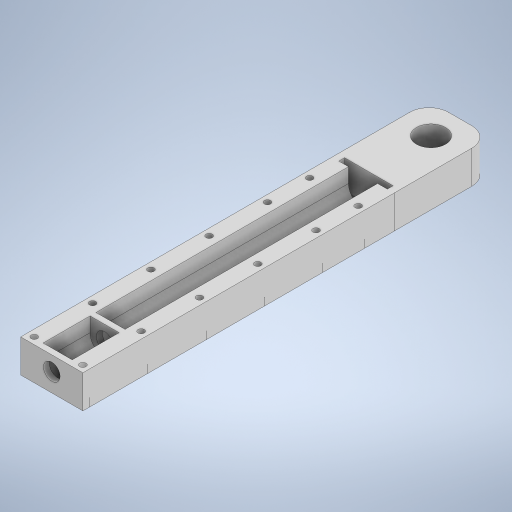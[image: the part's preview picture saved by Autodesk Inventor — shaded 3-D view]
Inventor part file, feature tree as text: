
AUTODESK INVENTOR PART (.ipt)
format: ipt  version: 2023 (Build 270158000, 158)  size: 453,120 bytes
history: native  units: mm
features: sketch x10, extrude x7, hole x3, fillet x1, projected_geometry x1
ambient origin geometry x8: Origin, YZ Plane, XZ Plane, XY Plane, X Axis, Y Axis, Z Axis, Center Point
bodies: Solid1 (feature_tree)
feature tree (22):
  extrude  "Extrusion1"  Depth=24.2mm TaperAngle=0.0deg
  extrude  "Extrusion3"  Depth=2.0mm
  extrude  "Extrusion4"  Depth=3.0mm TaperAngle=0.0deg
  extrude  "Extrusion5"  Depth=130.0mm TaperAngle=0.0deg
  hole  "Hole1"  [1 undecoded]
  hole  "Hole3"  [1 undecoded]
  extrude  "Extrusion6"  Depth=3.5mm
  extrude  "Extrusion7"  Depth=6.0mm
  fillet  "Fillet1"  Radius=50.0mm
  hole  "Hole4"  [1 undecoded]
  extrude  "Extrusion8"  Depth=20.0mm
  sketch  "Sketch1"  dims[d0=15.0mm d3=24.2mm d4=0.0mm]
  sketch  "Sketch2"  dims[d5=32.0mm d6=2.0mm]
  projected_geometry  "Projected Loop1"
  sketch  "Sketch4"  dims[d10=8.5mm d11=3.0mm d12=0.0mm]
  sketch  "Sketch5"  dims[d13=3.0mm d14=0.0mm d15=130.0mm d16=0.0mm]
  sketch  "Sketch6"  dims[d17=3.5mm d18=3.5mm]
  sketch  "Sketch7"  dims[d19=2.38125mm d20=6.0mm d21=4.0mm d22=2.0mm d23=90.0deg d24=10.0mm d25=20.594885mm d27=3.5mm]
  sketch  "Sketch8"  dims[d42=50.0mm d44=30.0mm d45=10.0mm d47=10.0mm d49=3.5mm]
  sketch  "Sketch9"  dims[d50=15.0mm]
  sketch  "Sketch10"  dims[d51=3.175mm d52=6.0mm d53=4.0mm d54=2.0mm d55=90.0deg d56=10.0mm d57=20.594885mm d58=6.0mm]
  sketch  "Sketch11"  dims[d59=20.0mm d61=25.0mm d62=10.0mm d64=10.0mm d66=50.0mm d68=30.0mm d69=10.0mm d71=10.0mm d73=50.0mm d75=30.0mm d76=10.0mm d78=10.0mm d80=20.0mm d82=21.5mm d83=10.0mm d85=10.0mm d87=4.0mm d88=0.0mm d89=50.0mm d90=0.0mm d91=10.0mm d94=15.0mm d95=15.0mm d96=6.0mm d97=4.0mm d98=2.0mm d99=90.0deg d100=8.0mm d101=20.594885mm d102=25.0mm d103=3.0mm d104=15.0mm d105=0.0mm]
note: 3 required parameter values undecoded (feature->parameter linkage not recoverable at this tier; creation-order binding heuristic only, values carry confidence <= 0.55)
